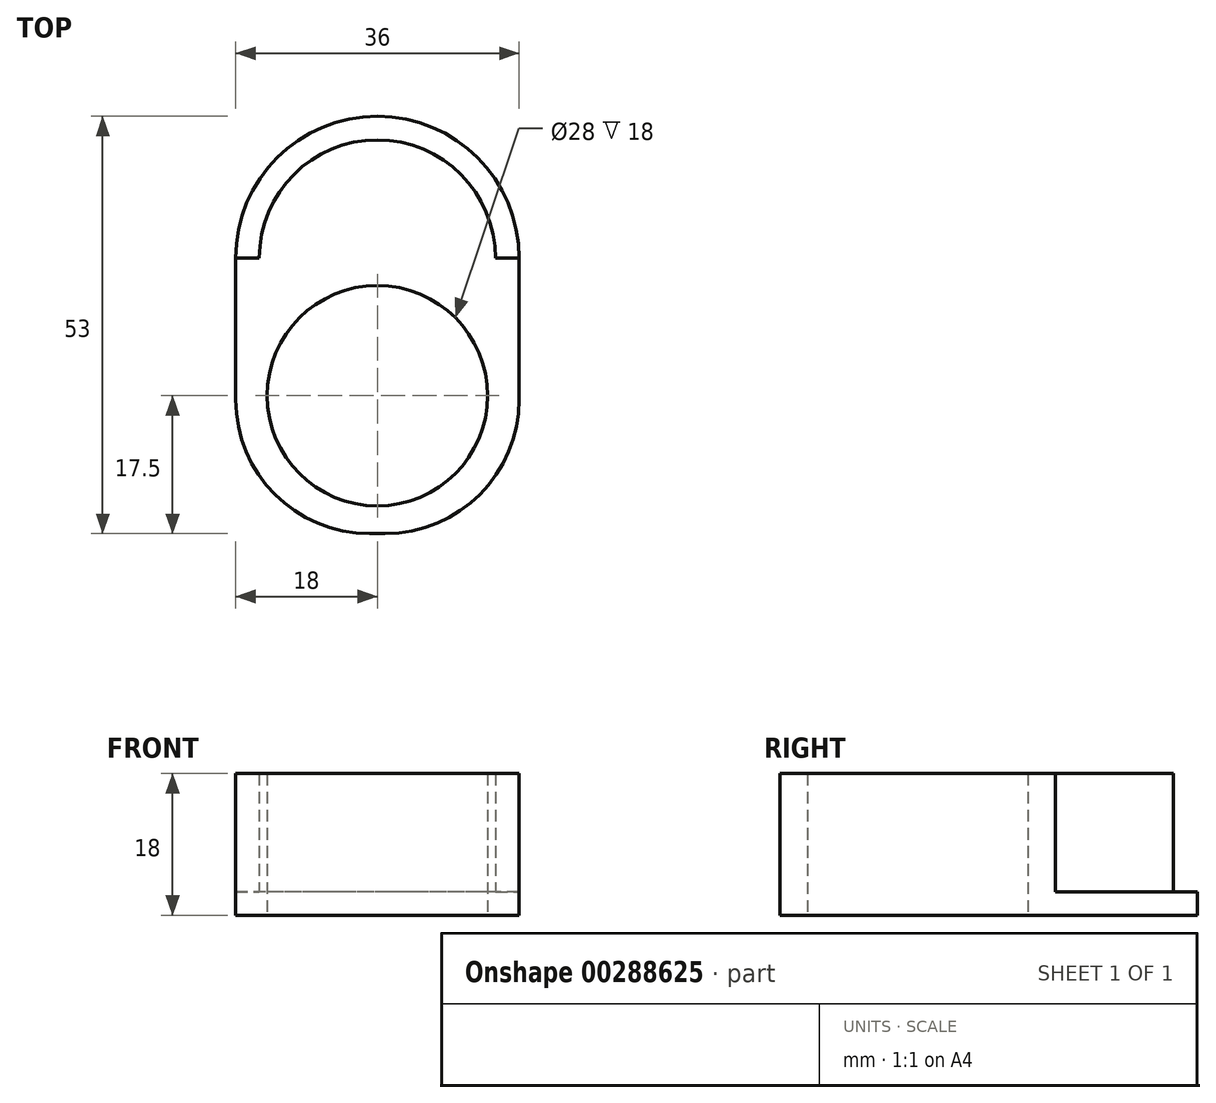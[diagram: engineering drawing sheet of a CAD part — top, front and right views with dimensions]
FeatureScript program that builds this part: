
annotation { "Feature Type Name" : "Feature", "Feature Type Description" : "" }
export const myFeature = defineFeature(function(context is Context, id is Id, definition is map)
    precondition{}
    {
        {
            var Q0;
            Q0=qCreatedBy(makeId("Top.planeOp"),FACE);
            var sketch = newSketch(context, id + "F0", { "sketchPlane" : qUnion([Q0])});
            skArc(sketch, "E0", {"start": v(18, 0) * mm, "mid": v(0, 18) * mm, "end": v(-18, 0) * mm});
            skLineSegment(sketch, "E1", {"start": v(-18, 0) * mm, "end": v(18, 0) * mm});
            skLineSegment(sketch, "E2.bottom", {"start": v(-18, 0) * mm, "end": v(18, 0) * mm, "construction": true});
            skLineSegment(sketch, "E2.top", {"start": v(-18, -35) * mm, "end": v(18, -35) * mm});
            skLineSegment(sketch, "E2.left", {"start": v(-18, 0) * mm, "end": v(-18, -35) * mm});
            skLineSegment(sketch, "E2.right", {"start": v(18, 0) * mm, "end": v(18, -35) * mm});
            skLineSegment(sketch, "E3", {"start": v(0, 0) * mm, "end": v(0, -35) * mm, "construction": true});
            skCircle(sketch, "E4", {"center": v(0, -17.5) * mm, "radius": 14 * mm});
            skSolve(sketch);
        }
        {
            var Q0;
            Q0=makeQuery(id+"F0.imprint","IMPRINT",FACE,{"disambiguationData":[TD([[makeQuery(id+"F0.imprint","IMPRINT",EDGE,{"derivedFrom":sQuery(id+"F0.wireOp",EDGE,"E1")}),-1.0]])]});
            var Q1;
            Q1=makeQuery(id+"F0.imprint","IMPRINT",FACE,{"disambiguationData":[TD([[makeQuery(id+"F0.imprint","IMPRINT",EDGE,{"derivedFrom":sQuery(id+"F0.wireOp",EDGE,"E0")}),1.0]])]});
            extrude(context, id + "F1", {"entities" : qUnion([Q0, Q1]), "depth" : 3 * mm});
        }
        {
            var Q0;
            Q0=makeQuery(id+"F1.opExtrude","CAP_FACE",FACE,{"disambiguationData":[OSD([sQuery(id+"F0.wireOp",EDGE,"E0"),sQuery(id+"F0.wireOp",EDGE,"E2.top"),sQuery(id+"F0.wireOp",EDGE,"E2.left"),sQuery(id+"F0.wireOp",EDGE,"E2.right"),sQuery(id+"F0.wireOp",EDGE,"E4")])],"isStart":false});
            var sketch = newSketch(context, id + "F2", { "sketchPlane" : qUnion([Q0])});
            skLineSegment(sketch, "E5.bottom", {"start": v(-18, 0) * mm, "end": v(18, 0) * mm});
            skLineSegment(sketch, "E5.top", {"start": v(-18, -35) * mm, "end": v(18, -35) * mm});
            skLineSegment(sketch, "E5.left", {"start": v(-18, 0) * mm, "end": v(-18, -35) * mm});
            skLineSegment(sketch, "E5.right", {"start": v(18, 0) * mm, "end": v(18, -35) * mm});
            skArc(sketch, "E6", {"start": v(15, 0) * mm, "mid": v(0, 15) * mm, "end": v(-15, 0) * mm});
            skCircle(sketch, "E7", {"center": v(0, -17.5) * mm, "radius": 14 * mm});
            skSolve(sketch);
        }
        {
            var Q0;
            {var subQ0=sQuery(id+"F2.wireOp",EDGE,"E6");Q0=makeQuery(id+"F2.imprint","IMPRINT",FACE,{"disambiguationData":[TD([[makeQuery(id+"F2.imprint","IMPRINT",EDGE,{"derivedFrom":subQ0}),1.0]])]});}
            var Q1;
            Q1=makeQuery(id+"F2.imprint","IMPRINT",FACE,{"disambiguationData":[TD([[makeQuery(id+"F2.imprint","IMPRINT",EDGE,{"derivedFrom":sQuery(id+"F2.wireOp",EDGE,"E5.top")}),1.0]])]});
            extrude(context, id + "F3", {"entities" : qUnion([Q0, Q1]), "operationType" : NewBodyOperationType.ADD, "depth" : 15 * mm});
        }
        {
            var Q0;
            Q0=makeQuery(id+"F3.boolean.opBoolean","MERGE",EDGE,{"derivedFrom":[makeQuery(id+"F1.opExtrude","SWEPT_EDGE",EDGE,{"disambiguationData":[OSD([sQuery(id+"F0.wireOp",EDGE,"E2.top"),sQuery(id+"F0.wireOp",EDGE,"E2.left")])]}),makeQuery(id+"F3.opExtrude","SWEPT_EDGE",EDGE,{"disambiguationData":[OSD([sQuery(id+"F2.wireOp",EDGE,"E5.top"),sQuery(id+"F2.wireOp",EDGE,"E5.left")])]})]});
            var Q1;
            Q1=makeQuery(id+"F3.boolean.opBoolean","MERGE",EDGE,{"derivedFrom":[makeQuery(id+"F1.opExtrude","SWEPT_EDGE",EDGE,{"disambiguationData":[OSD([sQuery(id+"F0.wireOp",EDGE,"E2.top"),sQuery(id+"F0.wireOp",EDGE,"E2.right")])]}),makeQuery(id+"F3.opExtrude","SWEPT_EDGE",EDGE,{"disambiguationData":[OSD([sQuery(id+"F2.wireOp",EDGE,"E5.top"),sQuery(id+"F2.wireOp",EDGE,"E5.right")])]})]});
            fillet(context, id + "F4", {"entities" : qUnion([Q0, Q1]), "radius" : 17 * mm, "tangentPropagation" : true, "allowEdgeOverflow" : false});
        }
    });
